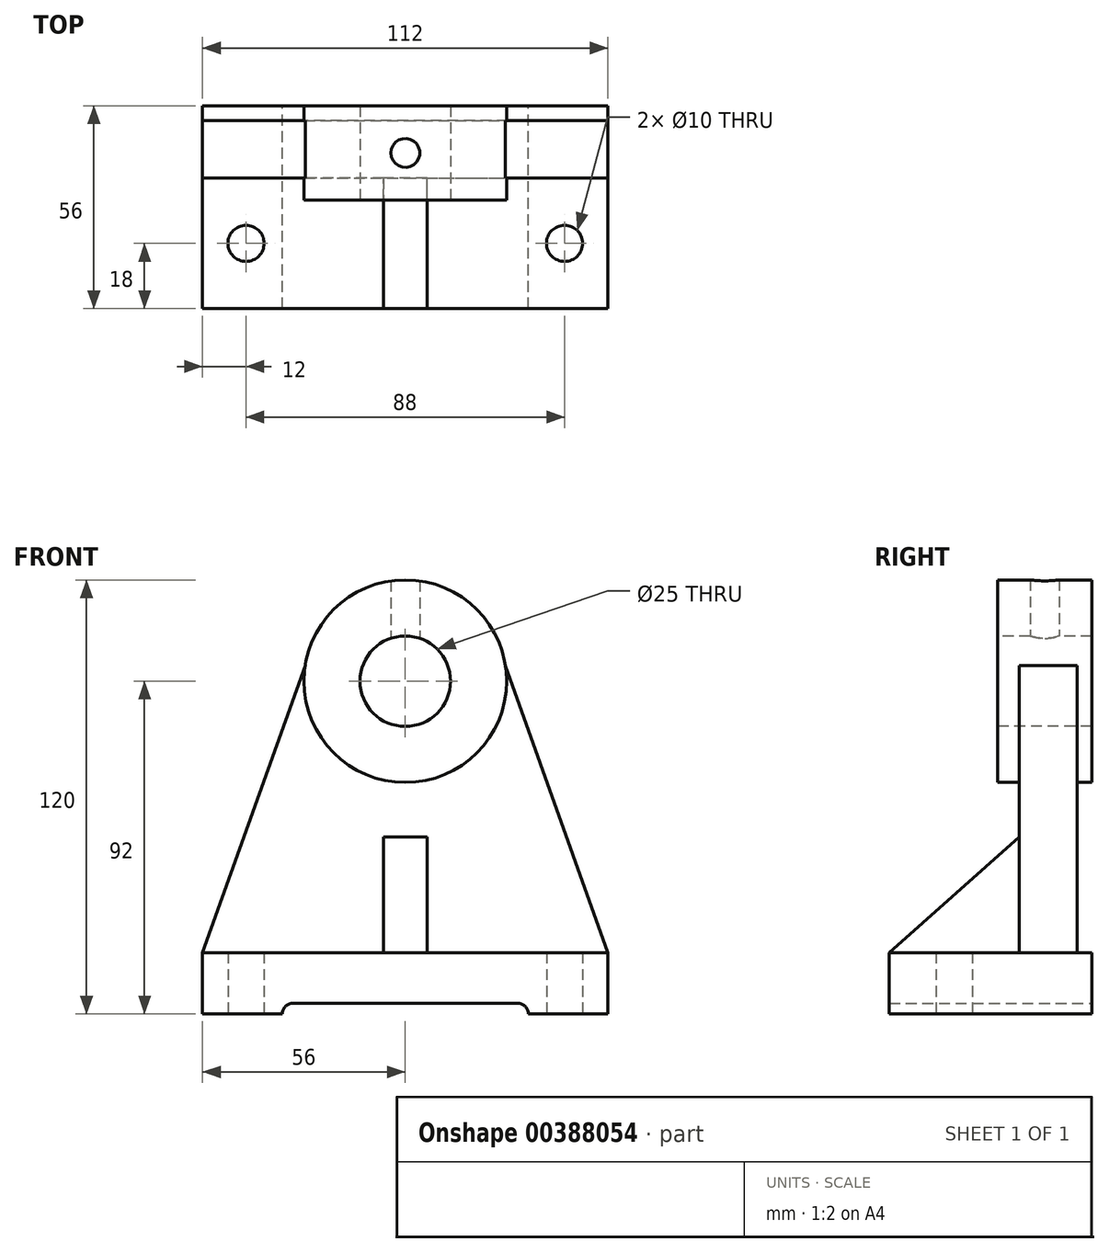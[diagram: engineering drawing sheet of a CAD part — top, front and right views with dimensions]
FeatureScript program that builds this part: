
annotation { "Feature Type Name" : "Feature", "Feature Type Description" : "" }
export const myFeature = defineFeature(function(context is Context, id is Id, definition is map)
    precondition{}
    {
        {
            var Q0;
            Q0=qCreatedBy(makeId("Front.planeOp"),FACE);
            var sketch = newSketch(context, id + "F0", { "sketchPlane" : qUnion([Q0])});
            skLineSegment(sketch, "E0.bottom", {"start": v(0, 0) * mm, "end": v(22, 0) * mm});
            skLineSegment(sketch, "E0.top", {"start": v(0, 17) * mm, "end": v(112, 17) * mm});
            skLineSegment(sketch, "E0.left", {"start": v(0, 0) * mm, "end": v(0, 17) * mm});
            skLineSegment(sketch, "E0.right", {"start": v(112, 0) * mm, "end": v(112, 17) * mm});
            skLineSegment(sketch, "E1.top", {"start": v(22, 3) * mm, "end": v(90, 3) * mm});
            skLineSegment(sketch, "E1.left", {"start": v(22, 0) * mm, "end": v(22, 3) * mm});
            skLineSegment(sketch, "E1.right", {"start": v(90, 0) * mm, "end": v(90, 3) * mm});
            skLineSegment(sketch, "E2.trimOffspring", {"start": v(90, 0) * mm, "end": v(112, 0) * mm});
            skSolve(sketch);
        }
        {
            var Q0;
            Q0 = qSketchRegion(id + "F0", true);
            extrude(context, id + "F1", {"entities" : qUnion([Q0]), "endBound" : BoundingType.SYMMETRIC, "depth" : 56 * mm});
        }
        {
            var Q0;
            Q0=qCreatedBy(makeId("Front.planeOp"),FACE);
            var sketch = newSketch(context, id + "F2", { "sketchPlane" : qUnion([Q0])});
            skLineSegment(sketch, "E3", {"start": v(0, 17) * mm, "end": v(28.33, 96.3) * mm});
            skLineSegment(sketch, "E4", {"start": v(112, 17) * mm, "end": v(83.67, 96.3) * mm});
            skLineSegment(sketch, "E5", {"start": v(0, 17) * mm, "end": v(112, 17) * mm});
            skArc(sketch, "E6", {"start": v(28.33, 96.3) * mm, "mid": v(56, 64) * mm, "end": v(83.67, 96.3) * mm});
            skSolve(sketch);
        }
        {
            var Q0;
            Q0 = qSketchRegion(id + "F2", true);
            extrude(context, id + "F3", {"entities" : qUnion([Q0]), "operationType" : NewBodyOperationType.ADD, "oppositeDirection" : true, "depth" : 28 * mm});
        }
        {
            var Q0;
            Q0=makeQuery(id+"F3.opExtrude","CAP_FACE",FACE,{"disambiguationData":[OSD([sQuery(id+"F2.wireOp",EDGE,"E3"),sQuery(id+"F2.wireOp",EDGE,"E4"),sQuery(id+"F2.wireOp",EDGE,"E5"),sQuery(id+"F2.wireOp",EDGE,"E6")])],"isStart":true});
            var sketch = newSketch(context, id + "F4", { "sketchPlane" : qUnion([Q0])});
            skLineSegment(sketch, "E7", {"start": v(28.33, 96.3) * mm, "end": v(0, 17) * mm});
            skLineSegment(sketch, "E8", {"start": v(0, 17) * mm, "end": v(112, 17) * mm});
            skLineSegment(sketch, "E9", {"start": v(112, 17) * mm, "end": v(83.67, 96.3) * mm});
            skArc(sketch, "E10", {"start": v(28.33, 96.3) * mm, "mid": v(56, 64) * mm, "end": v(83.67, 96.3) * mm});
            skSolve(sketch);
        }
        {
            var Q0;
            Q0 = qSketchRegion(id + "F4", true);
            extrude(context, id + "F5", {"entities" : qUnion([Q0]), "operationType" : NewBodyOperationType.REMOVE, "oppositeDirection" : true, "depth" : 8 * mm});
        }
        {
            var Q0;
            Q0=makeQuery(id+"F3.boolean.opBoolean","MERGE",FACE,{"derivedFrom":[makeQuery(id+"F1.opExtrude","CAP_FACE",FACE,{"disambiguationData":[OSD([sQuery(id+"F0.wireOp",EDGE,"E0.bottom"),sQuery(id+"F0.wireOp",EDGE,"E0.top"),sQuery(id+"F0.wireOp",EDGE,"E0.left"),sQuery(id+"F0.wireOp",EDGE,"E0.right"),sQuery(id+"F0.wireOp",EDGE,"E1.top"),sQuery(id+"F0.wireOp",EDGE,"E1.left"),sQuery(id+"F0.wireOp",EDGE,"E1.right"),sQuery(id+"F0.wireOp",EDGE,"E2.trimOffspring")])],"isStart":true}),makeQuery(id+"F3.opExtrude","CAP_FACE",FACE,{"disambiguationData":[OSD([sQuery(id+"F2.wireOp",EDGE,"E3"),sQuery(id+"F2.wireOp",EDGE,"E4"),sQuery(id+"F2.wireOp",EDGE,"E5"),sQuery(id+"F2.wireOp",EDGE,"E6")])],"isStart":false})]});
            var sketch = newSketch(context, id + "F6", { "sketchPlane" : qUnion([Q0])});
            skLineSegment(sketch, "E11", {"start": v(-112, 17) * mm, "end": v(-83.67, 96.3) * mm});
            skLineSegment(sketch, "E12", {"start": v(-28.33, 96.3) * mm, "end": v(0, 17) * mm});
            skLineSegment(sketch, "E13", {"start": v(-112, 17) * mm, "end": v(0, 17) * mm});
            skArc(sketch, "E14", {"start": v(-83.67, 96.3) * mm, "mid": v(-56, 64) * mm, "end": v(-28.33, 96.3) * mm});
            skSolve(sketch);
        }
        {
            var Q0;
            Q0 = qSketchRegion(id + "F6", true);
            extrude(context, id + "F7", {"entities" : qUnion([Q0]), "operationType" : NewBodyOperationType.REMOVE, "oppositeDirection" : true, "depth" : 4 * mm});
        }
        {
            var Q0;
            Q0=qCreatedBy(makeId("Front.planeOp"),FACE);
            var sketch = newSketch(context, id + "F8", { "sketchPlane" : qUnion([Q0])});
            skCircle(sketch, "E15", {"center": v(56, 92) * mm, "radius": 28 * mm});
            skSolve(sketch);
        }
        {
            var Q0;
            Q0 = qSketchRegion(id + "F8", true);
            extrude(context, id + "F9", {"entities" : qUnion([Q0]), "operationType" : NewBodyOperationType.ADD, "oppositeDirection" : true, "depth" : 28 * mm});
        }
        {
            var Q0;
            Q0=makeQuery(id+"F9.opExtrude","CAP_FACE",FACE,{"disambiguationData":[OSD([sQuery(id+"F8.wireOp",EDGE,"E15")])],"isStart":true});
            var sketch = newSketch(context, id + "F10", { "sketchPlane" : qUnion([Q0])});
            skCircle(sketch, "E16", {"center": v(56, 92) * mm, "radius": 28 * mm});
            skSolve(sketch);
        }
        {
            var Q0;
            Q0 = qSketchRegion(id + "F10", true);
            extrude(context, id + "F11", {"entities" : qUnion([Q0]), "operationType" : NewBodyOperationType.REMOVE, "oppositeDirection" : true, "depth" : 2 * mm});
        }
        {
            var Q0;
            Q0=makeQuery(id+"F11.boolean.opBoolean","COPY",FACE,{"derivedFrom":makeQuery(id+"F11.opExtrude","CAP_FACE",FACE,{"disambiguationData":[OSD([sQuery(id+"F10.wireOp",EDGE,"E16")])],"isStart":false})});
            var sketch = newSketch(context, id + "F12", { "sketchPlane" : qUnion([Q0])});
            skCircle(sketch, "E17", {"center": v(56, 92) * mm, "radius": 12.5 * mm});
            skSolve(sketch);
        }
        {
            var Q0;
            Q0 = qSketchRegion(id + "F12", true);
            extrude(context, id + "F13", {"entities" : qUnion([Q0]), "operationType" : NewBodyOperationType.REMOVE, "endBound" : BoundingType.THROUGH_ALL, "oppositeDirection" : true, "depth" : 25 * mm});
        }
        {
            var Q0;
            Q0=qCreatedBy(makeId("Right.planeOp"),FACE);
            var sketch = newSketch(context, id + "F14", { "sketchPlane" : qUnion([Q0])});
            skLineSegment(sketch, "E18", {"start": v(-28, 17) * mm, "end": v(8, 49) * mm});
            skLineSegment(sketch, "E19", {"start": v(-28, 17) * mm, "end": v(8, 17) * mm});
            skLineSegment(sketch, "E20", {"start": v(8, 17) * mm, "end": v(8, 49) * mm});
            skSolve(sketch);
        }
        {
            var Q0;
            Q0 = qSketchRegion(id + "F14", true);
            extrude(context, id + "F15", {"entities" : qUnion([Q0]), "operationType" : NewBodyOperationType.ADD, "depth" : 112 * mm});
        }
        {
            var Q0;
            Q0=makeQuery(id+"F15.boolean.opBoolean","MERGE",FACE,{"derivedFrom":[makeQuery(id+"F1.opExtrude","SWEPT_FACE",FACE,{"disambiguationData":[OSD([sQuery(id+"F0.wireOp",EDGE,"E0.right")])]}),makeQuery(id+"F15.opExtrude","CAP_FACE",FACE,{"disambiguationData":[OSD([sQuery(id+"F14.wireOp",EDGE,"E18"),sQuery(id+"F14.wireOp",EDGE,"E19"),sQuery(id+"F14.wireOp",EDGE,"E20")])],"isStart":false})]});
            var sketch = newSketch(context, id + "F16", { "sketchPlane" : qUnion([Q0])});
            skLineSegment(sketch, "E21", {"start": v(-28, 17) * mm, "end": v(8, 17) * mm});
            skLineSegment(sketch, "E22", {"start": v(8, 49) * mm, "end": v(8, 17) * mm});
            skLineSegment(sketch, "E23", {"start": v(-28, 17) * mm, "end": v(8, 49) * mm});
            skSolve(sketch);
        }
        {
            var Q0;
            Q0 = qSketchRegion(id + "F16", true);
            extrude(context, id + "F17", {"entities" : qUnion([Q0]), "operationType" : NewBodyOperationType.REMOVE, "oppositeDirection" : true, "depth" : 50 * mm});
        }
        {
            var Q0;
            Q0=makeQuery(id+"F15.boolean.opBoolean","MERGE",FACE,{"derivedFrom":[makeQuery(id+"F1.opExtrude","SWEPT_FACE",FACE,{"disambiguationData":[OSD([sQuery(id+"F0.wireOp",EDGE,"E0.left")])]}),makeQuery(id+"F15.opExtrude","CAP_FACE",FACE,{"disambiguationData":[OSD([sQuery(id+"F14.wireOp",EDGE,"E18"),sQuery(id+"F14.wireOp",EDGE,"E19"),sQuery(id+"F14.wireOp",EDGE,"E20")])],"isStart":true})]});
            var sketch = newSketch(context, id + "F18", { "sketchPlane" : qUnion([Q0])});
            skLineSegment(sketch, "E24", {"start": v(-8, 17) * mm, "end": v(28, 17) * mm});
            skLineSegment(sketch, "E25", {"start": v(28, 17) * mm, "end": v(-8, 49) * mm});
            skLineSegment(sketch, "E26", {"start": v(-8, 17) * mm, "end": v(-8, 49) * mm});
            skSolve(sketch);
        }
        {
            var Q0;
            Q0 = qSketchRegion(id + "F18", true);
            extrude(context, id + "F19", {"entities" : qUnion([Q0]), "operationType" : NewBodyOperationType.REMOVE, "oppositeDirection" : true, "depth" : 50 * mm});
        }
        {
            var Q0;
            Q0=qCreatedBy(makeId("Top.planeOp"),FACE);
            var sketch = newSketch(context, id + "F20", { "sketchPlane" : qUnion([Q0])});
            skCircle(sketch, "E27", {"center": v(56, 15) * mm, "radius": 4 * mm});
            skSolve(sketch);
        }
        {
            var Q0;
            Q0 = qSketchRegion(id + "F20", true);
            extrude(context, id + "F21", {"entities" : qUnion([Q0]), "operationType" : NewBodyOperationType.REMOVE, "depth" : 139 * mm});
        }
        {
            var Q0;
            Q0=qCreatedBy(makeId("Top.planeOp"),FACE);
            var sketch = newSketch(context, id + "F22", { "sketchPlane" : qUnion([Q0])});
            skCircle(sketch, "E28", {"center": v(56, 15) * mm, "radius": 4 * mm});
            skSolve(sketch);
        }
        {
            var Q0;
            Q0 = qSketchRegion(id + "F22", true);
            extrude(context, id + "F23", {"entities" : qUnion([Q0]), "operationType" : NewBodyOperationType.ADD, "depth" : 91 * mm});
        }
        {
            var Q0;
            Q0=makeQuery(id+"F11.boolean.opBoolean","COPY",FACE,{"derivedFrom":makeQuery(id+"F11.opExtrude","CAP_FACE",FACE,{"disambiguationData":[OSD([sQuery(id+"F10.wireOp",EDGE,"E16")])],"isStart":false})});
            var sketch = newSketch(context, id + "F24", { "sketchPlane" : qUnion([Q0])});
            skCircle(sketch, "E29", {"center": v(56, 92) * mm, "radius": 12.5 * mm});
            skSolve(sketch);
        }
        {
            var Q0;
            Q0 = qSketchRegion(id + "F24", true);
            extrude(context, id + "F25", {"entities" : qUnion([Q0]), "operationType" : NewBodyOperationType.REMOVE, "endBound" : BoundingType.THROUGH_ALL, "oppositeDirection" : true, "depth" : 25 * mm});
        }
        {
            var Q0;
            Q0=qCreatedBy(makeId("Top.planeOp"),FACE);
            var sketch = newSketch(context, id + "F26", { "sketchPlane" : qUnion([Q0])});
            skCircle(sketch, "E30", {"center": v(12, -10) * mm, "radius": 5 * mm});
            skCircle(sketch, "E31", {"center": v(100, -10) * mm, "radius": 5 * mm});
            skSolve(sketch);
        }
        {
            var Q0;
            Q0 = qSketchRegion(id + "F26", true);
            extrude(context, id + "F27", {"entities" : qUnion([Q0]), "operationType" : NewBodyOperationType.REMOVE, "endBound" : BoundingType.THROUGH_ALL, "depth" : 25 * mm});
        }
        {
            var Q0;
            Q0=qCreatedBy(makeId("Front.planeOp"),FACE);
            var sketch = newSketch(context, id + "F28", { "sketchPlane" : qUnion([Q0])});
            skLineSegment(sketch, "E32.bottom", {"start": v(22, 0) * mm, "end": v(90, 0) * mm});
            skLineSegment(sketch, "E32.top", {"start": v(22, 3) * mm, "end": v(90, 3) * mm});
            skLineSegment(sketch, "E32.left", {"start": v(22, 0) * mm, "end": v(22, 3) * mm});
            skLineSegment(sketch, "E32.right", {"start": v(90, 0) * mm, "end": v(90, 3) * mm});
            skSolve(sketch);
        }
        {
            var Q0;
            Q0 = qSketchRegion(id + "F28", true);
            extrude(context, id + "F29", {"entities" : qUnion([Q0]), "operationType" : NewBodyOperationType.REMOVE, "endBound" : BoundingType.THROUGH_ALL, "oppositeDirection" : true, "depth" : 25 * mm});
        }
        {
            var Q0;
            Q0=makeQuery(id+"F1.opExtrude","SWEPT_EDGE",EDGE,{"disambiguationData":[OSD([sQuery(id+"F0.wireOp",EDGE,"E1.top"),sQuery(id+"F0.wireOp",EDGE,"E1.right")])]});
            var Q1;
            Q1=makeQuery(id+"F1.opExtrude","SWEPT_EDGE",EDGE,{"disambiguationData":[OSD([sQuery(id+"F0.wireOp",EDGE,"E1.top"),sQuery(id+"F0.wireOp",EDGE,"E1.left")])]});
            fillet(context, id + "F30", {"entities" : qUnion([Q0, Q1]), "radius" : 3 * mm, "tangentPropagation" : true, "allowEdgeOverflow" : false});
        }
    });
